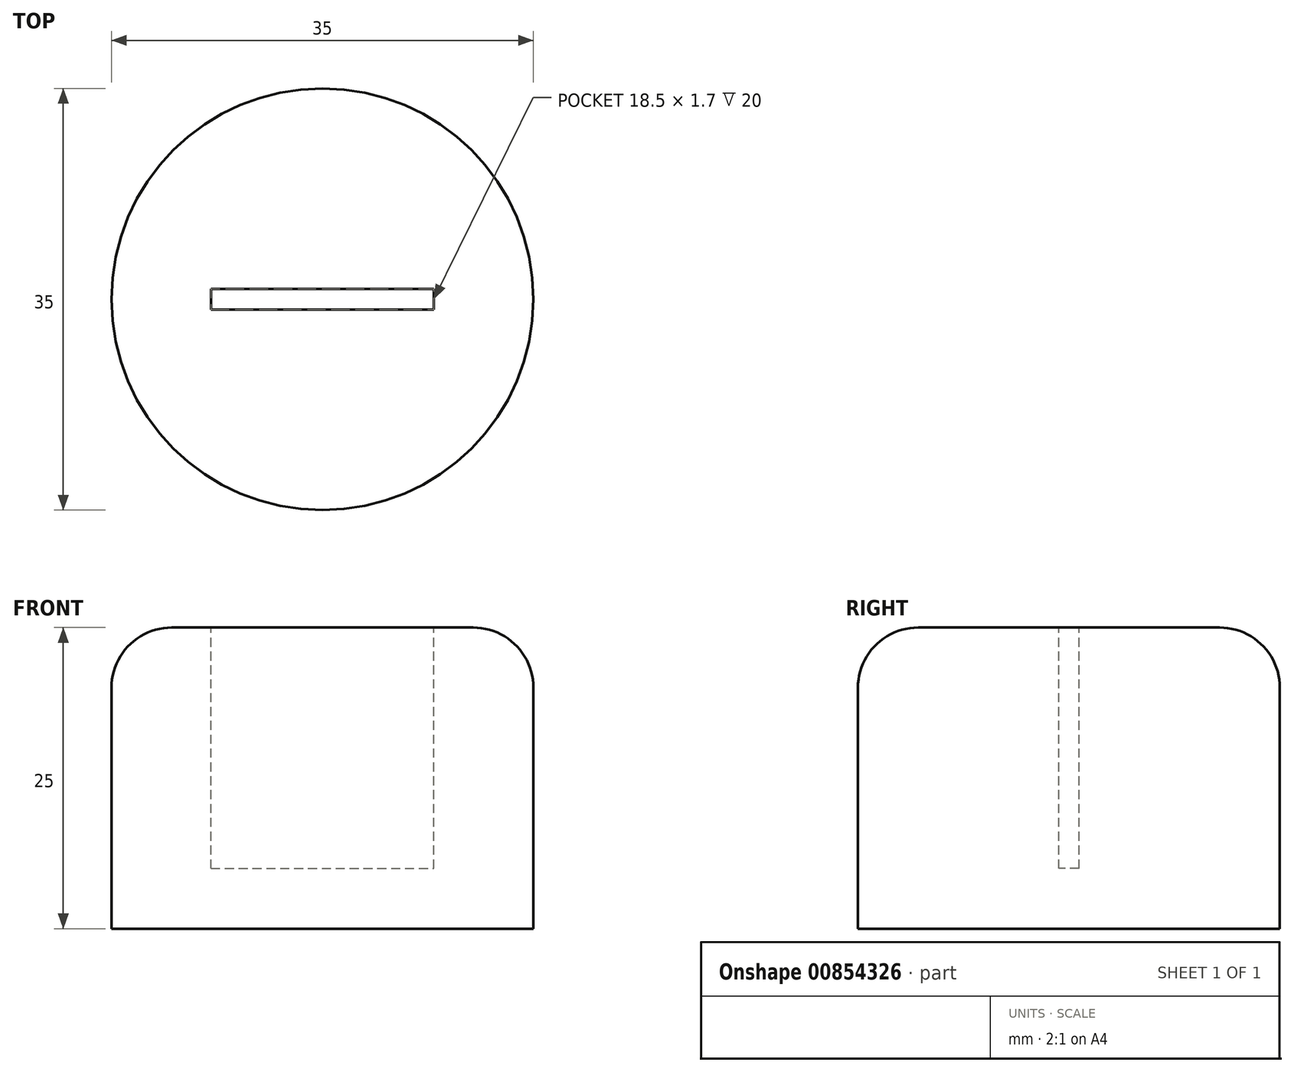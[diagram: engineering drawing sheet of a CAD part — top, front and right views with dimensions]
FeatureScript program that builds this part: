
annotation { "Feature Type Name" : "Feature", "Feature Type Description" : "" }
export const myFeature = defineFeature(function(context is Context, id is Id, definition is map)
    precondition{}
    {
        {
            var Q0;
            Q0=qCreatedBy(makeId("Top.planeOp"),FACE);
            var sketch = newSketch(context, id + "F0", { "sketchPlane" : qUnion([Q0])});
            skCircle(sketch, "E0", {"center": v(0, 0) * mm, "radius": 17.5 * mm});
            skSolve(sketch);
        }
        {
            var Q0;
            Q0=makeQuery(id+"F0.imprint","IMPRINT",FACE,{"disambiguationData":[TD([[makeQuery(id+"F0.imprint","IMPRINT",EDGE,{"derivedFrom":sQuery(id+"F0.wireOp",EDGE,"E0")}),1.0]])]});
            extrude(context, id + "F1", {"entities" : qUnion([Q0]), "depth" : 25 * mm, "offsetDistance" : 25 * mm});
        }
        {
            var Q0;
            Q0=makeQuery(id+"F1.opExtrude","CAP_EDGE",EDGE,{"disambiguationData":[OSD([sQuery(id+"F0.wireOp",EDGE,"E0")])],"isStart":false});
            fillet(context, id + "F2", {"entities" : qUnion([Q0]), "radius" : 5 * mm, "tangentPropagation" : true, "allowEdgeOverflow" : false});
        }
        {
            var Q0;
            Q0=makeQuery(id+"F1.opExtrude","CAP_FACE",FACE,{"disambiguationData":[OSD([sQuery(id+"F0.wireOp",EDGE,"E0")])],"isStart":false});
            var sketch = newSketch(context, id + "F3", { "sketchPlane" : qUnion([Q0])});
            skLineSegment(sketch, "E1.bottom", {"start": v(-9.25, 0.85) * mm, "end": v(9.25, 0.85) * mm});
            skLineSegment(sketch, "E1.top", {"start": v(-9.25, -0.85) * mm, "end": v(9.25, -0.85) * mm});
            skLineSegment(sketch, "E1.left", {"start": v(-9.25, 0.85) * mm, "end": v(-9.25, -0.85) * mm});
            skLineSegment(sketch, "E1.right", {"start": v(9.25, 0.85) * mm, "end": v(9.25, -0.85) * mm});
            skPoint(sketch, "E1.middle", {"position": v(0, 0) * mm});
            skSolve(sketch);
        }
        {
            var Q0;
            Q0=makeQuery(id+"F3.imprint","IMPRINT",FACE,{"disambiguationData":[TD([[makeQuery(id+"F3.imprint","IMPRINT",EDGE,{"derivedFrom":sQuery(id+"F3.wireOp",EDGE,"E1.bottom")}),-1.0]])]});
            extrude(context, id + "F4", {"entities" : qUnion([Q0]), "operationType" : NewBodyOperationType.REMOVE, "oppositeDirection" : true, "depth" : 20 * mm, "offsetDistance" : 25 * mm});
        }
    });
